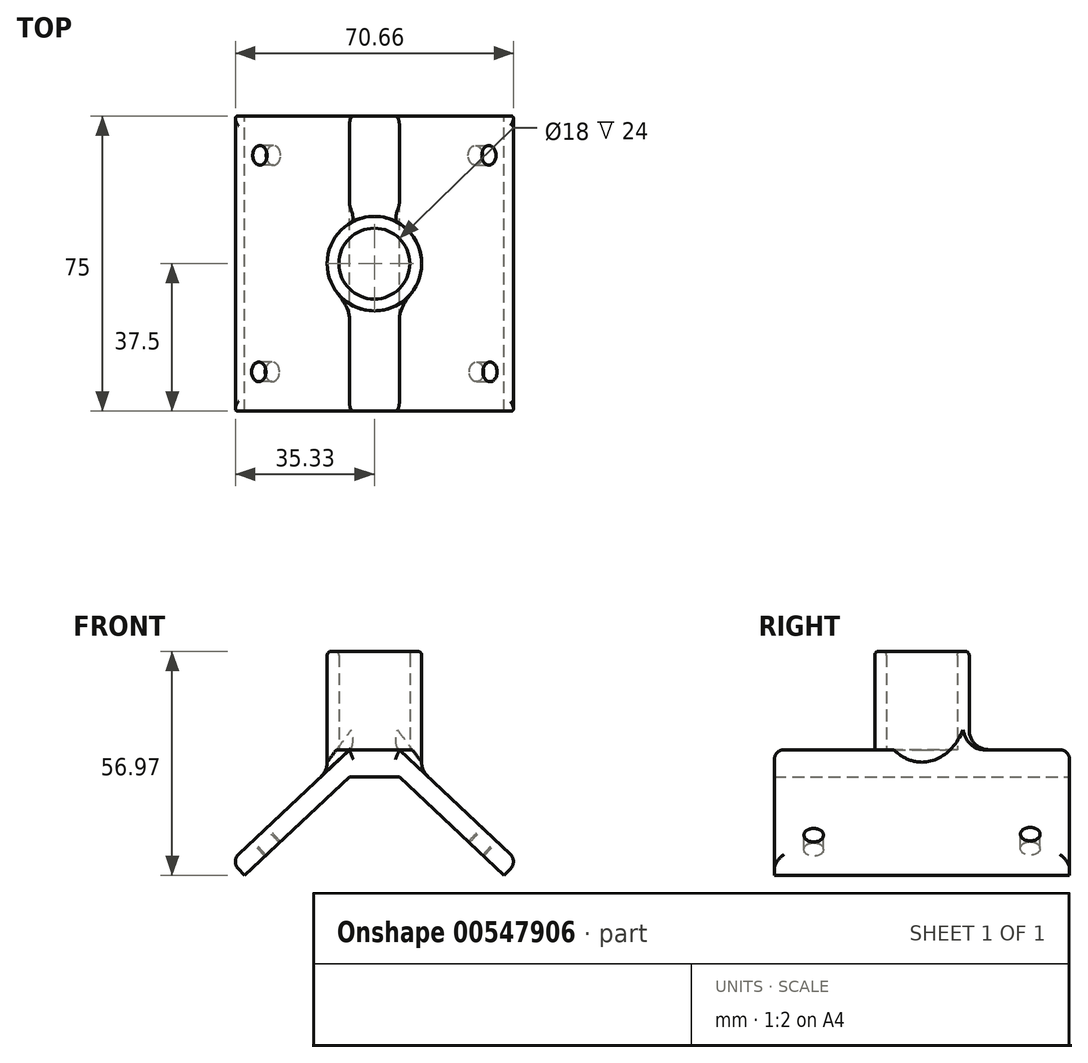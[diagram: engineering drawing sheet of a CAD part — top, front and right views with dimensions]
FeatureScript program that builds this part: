
annotation { "Feature Type Name" : "Feature", "Feature Type Description" : "" }
export const myFeature = defineFeature(function(context is Context, id is Id, definition is map)
    precondition{}
    {
        {
            var Q0;
            Q0=qCreatedBy(makeId("Front.planeOp"),FACE);
            var sketch = newSketch(context, id + "F0", { "sketchPlane" : qUnion([Q0])});
            skLineSegment(sketch, "E0", {"start": v(-6.35, 0) * mm, "end": v(6.35, 0) * mm});
            skLineSegment(sketch, "E1", {"start": v(6.35, 0) * mm, "end": v(107.95, -95.88) * mm});
            skLineSegment(sketch, "E2", {"start": v(107.95, -95.88) * mm, "end": v(-107.95, -95.88) * mm});
            skLineSegment(sketch, "E3", {"start": v(-107.95, -95.88) * mm, "end": v(-6.35, 0) * mm});
            skPoint(sketch, "E4", {"position": v(0, -95.88) * mm});
            skLineSegment(sketch, "E5", {"start": v(-32.93, -25.09) * mm, "end": v(-36.36, -21.45) * mm});
            skLineSegment(sketch, "E6", {"start": v(-36.36, -21.45) * mm, "end": v(0, 12.87) * mm});
            skLineSegment(sketch, "E7", {"start": v(0, 12.87) * mm, "end": v(0, 0) * mm});
            skLineSegment(sketch, "E8", {"start": v(-6.35, 6.88) * mm, "end": v(0, 6.88) * mm});
            skSolve(sketch);
        }
        {
            var Q0;
            {var subQ1=sQuery(id+"F0.wireOp",EDGE,"E5");Q0=makeQuery(id+"F0.imprint","IMPRINT",FACE,{"disambiguationData":[TD([[makeQuery(id+"F0.imprint","IMPRINT",EDGE,{"derivedFrom":subQ1}),-1.0]])]});}
            extrude(context, id + "F1", {"entities" : qUnion([Q0]), "endBound" : BoundingType.SYMMETRIC, "depth" : 75 * mm, "offsetDistance" : 25 * mm});
        }
        {
            var Q0;
            Q0=makeQuery(id+"F1.opExtrude","SWEPT_FACE",FACE,{"disambiguationData":[OSD([sQuery(id+"F0.wireOp",EDGE,"E6")])]});
            var sketch = newSketch(context, id + "F2", { "sketchPlane" : qUnion([Q0])});
            skLineSegment(sketch, "E9", {"start": v(-31.17, 37.5) * mm, "end": v(-31.17, 27.5) * mm, "construction": true});
            skLineSegment(sketch, "E10", {"start": v(-31.17, 27.5) * mm, "end": v(-41.17, 27.5) * mm, "construction": true});
            skCircle(sketch, "E11", {"center": v(-31.17, 27.5) * mm, "radius": 2.5 * mm});
            skLineSegment(sketch, "E12", {"start": v(-31.17, -37.5) * mm, "end": v(-31.55, -27.5) * mm, "construction": true});
            skLineSegment(sketch, "E13", {"start": v(-31.55, -27.5) * mm, "end": v(-41.17, -27.88) * mm, "construction": true});
            skCircle(sketch, "E14", {"center": v(-31.55, -27.5) * mm, "radius": 2.5 * mm});
            skSolve(sketch);
        }
        {
            var Q0;
            Q0=makeQuery(id+"F2.imprint","IMPRINT",FACE,{"disambiguationData":[TD([[makeQuery(id+"F2.imprint","IMPRINT",EDGE,{"derivedFrom":sQuery(id+"F2.wireOp",EDGE,"E11")}),1.0]])]});
            var Q1;
            Q1=makeQuery(id+"F2.imprint","IMPRINT",FACE,{"disambiguationData":[TD([[makeQuery(id+"F2.imprint","IMPRINT",EDGE,{"derivedFrom":sQuery(id+"F2.wireOp",EDGE,"E14")}),1.0]])]});
            extrude(context, id + "F3", {"entities" : qUnion([Q0, Q1]), "operationType" : NewBodyOperationType.REMOVE, "oppositeDirection" : true, "depth" : 25 * mm, "offsetDistance" : 25 * mm});
        }
        {
            var Q0;
            Q0=makeQuery(id+"F1.opExtrude","SWEPT_BODY",BODY,{"disambiguationData":[OSD([sQuery(id+"F0.wireOp",EDGE,"E0"),sQuery(id+"F0.wireOp",EDGE,"E3"),sQuery(id+"F0.wireOp",EDGE,"E5"),sQuery(id+"F0.wireOp",EDGE,"E6"),sQuery(id+"F0.wireOp",EDGE,"E7"),sQuery(id+"F0.wireOp",EDGE,"E8")])]});
            var Q1;
            Q1=qCreatedBy(makeId("Right.planeOp"),FACE);
            mirror(context, id + "F4", {"operationType" : NewBodyOperationType.ADD, "entities" : qUnion([Q0]), "mirrorPlane" : qUnion([Q1])});
        }
        {
            var Q0;
            {var subQ0=makeQuery(id+"F1.opExtrude","SWEPT_FACE",FACE,{"disambiguationData":[OSD([sQuery(id+"F0.wireOp",EDGE,"E8")])]});Q0=makeQuery(id+"F4.boolean.opBoolean","MERGE",FACE,{"derivedFrom":[subQ0,makeQuery(id+"F4.opPattern","COPY",FACE,{"derivedFrom":subQ0,"instanceName":"1"})]});}
            var sketch = newSketch(context, id + "F5", { "sketchPlane" : qUnion([Q0])});
            skCircle(sketch, "E15", {"center": v(0, 0) * mm, "radius": 9 * mm});
            skCircle(sketch, "E16", {"center": v(0, 0) * mm, "radius": 12 * mm});
            skSolve(sketch);
        }
        {
            var Q0;
            {var subQ0=sQuery(id+"F5.wireOp",EDGE,"E15");var subQ1=makeQuery(id+"F4.opPattern","COPY",EDGE,{"derivedFrom":makeQuery(id+"F1.opExtrude","SWEPT_EDGE",EDGE,{"disambiguationData":[OSD([sQuery(id+"F0.wireOp",EDGE,"E6"),sQuery(id+"F0.wireOp",EDGE,"E8")])]}),"instanceName":"1"});var subQ2=makeQuery(id+"F5.imprint","INTERSECT",VERTEX,{"disambiguationData":[OD(0.0)],"derivedFrom":[subQ1,subQ0]});Q0=makeQuery(id+"F5.imprint","IMPRINT",FACE,{"disambiguationData":[TD([[makeQuery(id+"F5.imprint","IMPRINT",EDGE,{"disambiguationData":[TD([[subQ2,1.0]])],"derivedFrom":subQ0}),-1.0]])]});}
            var Q1;
            {var subQ0=sQuery(id+"F5.wireOp",EDGE,"E15");var subQ1=makeQuery(id+"F1.opExtrude","SWEPT_EDGE",EDGE,{"disambiguationData":[OSD([sQuery(id+"F0.wireOp",EDGE,"E6"),sQuery(id+"F0.wireOp",EDGE,"E8")])]});var subQ2=makeQuery(id+"F5.imprint","INTERSECT",VERTEX,{"disambiguationData":[OD(1.0)],"derivedFrom":[subQ1,subQ0]});Q1=makeQuery(id+"F5.imprint","IMPRINT",FACE,{"disambiguationData":[TD([[makeQuery(id+"F5.imprint","IMPRINT",EDGE,{"disambiguationData":[TD([[subQ2,-1.0]])],"derivedFrom":subQ0}),-1.0]])]});}
            var Q2;
            {var subQ0=sQuery(id+"F5.wireOp",EDGE,"E15");var subQ1=makeQuery(id+"F1.opExtrude","SWEPT_EDGE",EDGE,{"disambiguationData":[OSD([sQuery(id+"F0.wireOp",EDGE,"E6"),sQuery(id+"F0.wireOp",EDGE,"E8")])]});var subQ2=makeQuery(id+"F5.imprint","INTERSECT",VERTEX,{"disambiguationData":[OD(0.0)],"derivedFrom":[subQ1,subQ0]});Q2=makeQuery(id+"F5.imprint","IMPRINT",FACE,{"disambiguationData":[TD([[makeQuery(id+"F5.imprint","IMPRINT",EDGE,{"disambiguationData":[TD([[subQ2,1.0]])],"derivedFrom":subQ0}),-1.0]])]});}
            var Q3;
            {var subQ0=sQuery(id+"F5.wireOp",EDGE,"E15");var subQ1=makeQuery(id+"F1.opExtrude","SWEPT_EDGE",EDGE,{"disambiguationData":[OSD([sQuery(id+"F0.wireOp",EDGE,"E6"),sQuery(id+"F0.wireOp",EDGE,"E8")])]});var subQ2=makeQuery(id+"F5.imprint","INTERSECT",VERTEX,{"disambiguationData":[OD(0.0)],"derivedFrom":[subQ1,subQ0]});Q3=makeQuery(id+"F5.imprint","IMPRINT",FACE,{"disambiguationData":[TD([[makeQuery(id+"F5.imprint","IMPRINT",EDGE,{"disambiguationData":[TD([[subQ2,-1.0]])],"derivedFrom":subQ0}),-1.0]])]});}
            var Q4;
            {var subQ0=sQuery(id+"F5.wireOp",EDGE,"E15");var subQ1=makeQuery(id+"F1.opExtrude","SWEPT_EDGE",EDGE,{"disambiguationData":[OSD([sQuery(id+"F0.wireOp",EDGE,"E6"),sQuery(id+"F0.wireOp",EDGE,"E8")])]});var subQ2=makeQuery(id+"F5.imprint","INTERSECT",VERTEX,{"disambiguationData":[OD(0.0)],"derivedFrom":[subQ1,subQ0]});Q4=makeQuery(id+"F5.imprint","IMPRINT",FACE,{"disambiguationData":[TD([[makeQuery(id+"F5.imprint","IMPRINT",EDGE,{"disambiguationData":[TD([[subQ2,-1.0]])],"derivedFrom":subQ0}),1.0]])]});}
            var Q5;
            {var subQ0=sQuery(id+"F5.wireOp",EDGE,"E15");var subQ1=makeQuery(id+"F4.opPattern","COPY",EDGE,{"derivedFrom":makeQuery(id+"F1.opExtrude","SWEPT_EDGE",EDGE,{"disambiguationData":[OSD([sQuery(id+"F0.wireOp",EDGE,"E6"),sQuery(id+"F0.wireOp",EDGE,"E8")])]}),"instanceName":"1"});var subQ2=makeQuery(id+"F5.imprint","INTERSECT",VERTEX,{"disambiguationData":[OD(0.0)],"derivedFrom":[subQ1,subQ0]});Q5=makeQuery(id+"F5.imprint","IMPRINT",FACE,{"disambiguationData":[TD([[makeQuery(id+"F5.imprint","IMPRINT",EDGE,{"disambiguationData":[TD([[subQ2,1.0]])],"derivedFrom":subQ0}),1.0]])]});}
            var Q6;
            {var subQ0=makeQuery(id+"F1.opExtrude","SWEPT_FACE",FACE,{"disambiguationData":[OSD([sQuery(id+"F0.wireOp",EDGE,"E0")])]});Q6=makeQuery(id+"F4.boolean.opBoolean","MERGE",FACE,{"derivedFrom":[subQ0,makeQuery(id+"F4.opPattern","COPY",FACE,{"derivedFrom":subQ0,"instanceName":"1"})]});}
            extrude(context, id + "F6", {"entities" : qUnion([Q0, Q1, Q2, Q3, Q4, Q5]), "operationType" : NewBodyOperationType.ADD, "endBound" : BoundingType.UP_TO_SURFACE, "oppositeDirection" : true, "depth" : 25 * mm, "endBoundEntityFace" : qUnion([Q6]), "offsetDistance" : 25 * mm});
        }
        {
            var Q0;
            {var subQ0=sQuery(id+"F5.wireOp",EDGE,"E15");var subQ1=makeQuery(id+"F1.opExtrude","SWEPT_EDGE",EDGE,{"disambiguationData":[OSD([sQuery(id+"F0.wireOp",EDGE,"E6"),sQuery(id+"F0.wireOp",EDGE,"E8")])]});var subQ2=makeQuery(id+"F5.imprint","INTERSECT",VERTEX,{"disambiguationData":[OD(0.0)],"derivedFrom":[subQ1,subQ0]});Q0=makeQuery(id+"F5.imprint","IMPRINT",FACE,{"disambiguationData":[TD([[makeQuery(id+"F5.imprint","IMPRINT",EDGE,{"disambiguationData":[TD([[subQ2,-1.0]])],"derivedFrom":subQ0}),-1.0]])]});}
            var Q1;
            {var subQ0=sQuery(id+"F5.wireOp",EDGE,"E15");var subQ1=makeQuery(id+"F1.opExtrude","SWEPT_EDGE",EDGE,{"disambiguationData":[OSD([sQuery(id+"F0.wireOp",EDGE,"E6"),sQuery(id+"F0.wireOp",EDGE,"E8")])]});var subQ2=makeQuery(id+"F5.imprint","INTERSECT",VERTEX,{"disambiguationData":[OD(0.0)],"derivedFrom":[subQ1,subQ0]});Q1=makeQuery(id+"F5.imprint","IMPRINT",FACE,{"disambiguationData":[TD([[makeQuery(id+"F5.imprint","IMPRINT",EDGE,{"disambiguationData":[TD([[subQ2,1.0]])],"derivedFrom":subQ0}),-1.0]])]});}
            var Q2;
            {var subQ0=sQuery(id+"F5.wireOp",EDGE,"E15");var subQ1=makeQuery(id+"F4.opPattern","COPY",EDGE,{"derivedFrom":makeQuery(id+"F1.opExtrude","SWEPT_EDGE",EDGE,{"disambiguationData":[OSD([sQuery(id+"F0.wireOp",EDGE,"E6"),sQuery(id+"F0.wireOp",EDGE,"E8")])]}),"instanceName":"1"});var subQ2=makeQuery(id+"F5.imprint","INTERSECT",VERTEX,{"disambiguationData":[OD(0.0)],"derivedFrom":[subQ1,subQ0]});Q2=makeQuery(id+"F5.imprint","IMPRINT",FACE,{"disambiguationData":[TD([[makeQuery(id+"F5.imprint","IMPRINT",EDGE,{"disambiguationData":[TD([[subQ2,1.0]])],"derivedFrom":subQ0}),-1.0]])]});}
            var Q3;
            {var subQ0=sQuery(id+"F5.wireOp",EDGE,"E15");var subQ1=makeQuery(id+"F1.opExtrude","SWEPT_EDGE",EDGE,{"disambiguationData":[OSD([sQuery(id+"F0.wireOp",EDGE,"E6"),sQuery(id+"F0.wireOp",EDGE,"E8")])]});var subQ2=makeQuery(id+"F5.imprint","INTERSECT",VERTEX,{"disambiguationData":[OD(1.0)],"derivedFrom":[subQ1,subQ0]});Q3=makeQuery(id+"F5.imprint","IMPRINT",FACE,{"disambiguationData":[TD([[makeQuery(id+"F5.imprint","IMPRINT",EDGE,{"disambiguationData":[TD([[subQ2,-1.0]])],"derivedFrom":subQ0}),-1.0]])]});}
            extrude(context, id + "F7", {"entities" : qUnion([Q0, Q1, Q2, Q3]), "operationType" : NewBodyOperationType.ADD, "depth" : 25 * mm, "offsetDistance" : 25 * mm});
        }
        {
            var Q0;
            Q0=makeQuery(id+"F7.opExtrude","CAP_EDGE",EDGE,{"disambiguationData":[OSD([sQuery(id+"F5.wireOp",EDGE,"E16")])],"isStart":false});
            var Q1;
            Q1=makeQuery(id+"F7.opExtrude","CAP_EDGE",EDGE,{"disambiguationData":[OSD([sQuery(id+"F5.wireOp",EDGE,"E15")])],"isStart":false});
            fillet(context, id + "F8", {"entities" : qUnion([Q0, Q1]), "tangentPropagation" : true, "radius" : 1 * mm, "defaultsChanged" : false, "vertexSettings" : [], "allowEdgeOverflow" : false});
        }
        {
            var Q0;
            Q0=makeQuery(id+"F6.boolean.opBoolean","INTERSECT",EDGE,{"derivedFrom":[makeQuery(id+"F1.opExtrude","SWEPT_FACE",FACE,{"disambiguationData":[OSD([sQuery(id+"F0.wireOp",EDGE,"E6")])]}),makeQuery(id+"F6.opExtrude","SWEPT_FACE",FACE,{"disambiguationData":[OSD([sQuery(id+"F5.wireOp",EDGE,"E16")])]})]});
            var Q1;
            Q1=makeQuery(id+"F7.boolean.opBoolean","SPLIT",EDGE,{"disambiguationData":[OD(1.0)],"derivedFrom":makeQuery(id+"F7.opExtrude","CAP_EDGE",EDGE,{"disambiguationData":[OSD([sQuery(id+"F5.wireOp",EDGE,"E16")])],"isStart":true})});
            var Q2;
            Q2=makeQuery(id+"F6.boolean.opBoolean","INTERSECT",EDGE,{"derivedFrom":[makeQuery(id+"F4.opPattern","COPY",FACE,{"derivedFrom":makeQuery(id+"F1.opExtrude","SWEPT_FACE",FACE,{"disambiguationData":[OSD([sQuery(id+"F0.wireOp",EDGE,"E6")])]}),"instanceName":"1"}),makeQuery(id+"F6.opExtrude","SWEPT_FACE",FACE,{"disambiguationData":[OSD([sQuery(id+"F5.wireOp",EDGE,"E16")])]})]});
            var Q3;
            Q3=makeQuery(id+"F7.boolean.opBoolean","SPLIT",EDGE,{"disambiguationData":[OD(0.0)],"derivedFrom":makeQuery(id+"F7.opExtrude","CAP_EDGE",EDGE,{"disambiguationData":[OSD([sQuery(id+"F5.wireOp",EDGE,"E16")])],"isStart":true})});
            fillet(context, id + "F9", {"entities" : qUnion([Q0, Q1, Q2, Q3]), "tangentPropagation" : true, "radius" : 5 * mm, "defaultsChanged" : false, "vertexSettings" : [], "allowEdgeOverflow" : false});
        }
        {
            var Q0;
            Q0=makeQuery(id+"F1.opExtrude","CAP_EDGE",EDGE,{"disambiguationData":[OSD([sQuery(id+"F0.wireOp",EDGE,"E6")])],"isStart":true});
            var Q1;
            Q1=makeQuery(id+"F1.opExtrude","SWEPT_EDGE",EDGE,{"disambiguationData":[OSD([sQuery(id+"F0.wireOp",EDGE,"E5"),sQuery(id+"F0.wireOp",EDGE,"E6")])]});
            var Q2;
            Q2=makeQuery(id+"F1.opExtrude","CAP_EDGE",EDGE,{"disambiguationData":[OSD([sQuery(id+"F0.wireOp",EDGE,"E6")])],"isStart":false});
            var Q3;
            {var subQ0=makeQuery(id+"F1.opExtrude","CAP_EDGE",EDGE,{"disambiguationData":[OSD([sQuery(id+"F0.wireOp",EDGE,"E8")])],"isStart":false});Q3=makeQuery(id+"F4.boolean.opBoolean","MERGE",EDGE,{"derivedFrom":[subQ0,makeQuery(id+"F4.opPattern","COPY",EDGE,{"derivedFrom":subQ0,"instanceName":"1"})]});}
            var Q4;
            Q4=makeQuery(id+"F4.opPattern","COPY",EDGE,{"derivedFrom":makeQuery(id+"F1.opExtrude","CAP_EDGE",EDGE,{"disambiguationData":[OSD([sQuery(id+"F0.wireOp",EDGE,"E6")])],"isStart":false}),"instanceName":"1"});
            var Q5;
            Q5=makeQuery(id+"F4.opPattern","COPY",EDGE,{"derivedFrom":makeQuery(id+"F1.opExtrude","SWEPT_EDGE",EDGE,{"disambiguationData":[OSD([sQuery(id+"F0.wireOp",EDGE,"E5"),sQuery(id+"F0.wireOp",EDGE,"E6")])]}),"instanceName":"1"});
            var Q6;
            Q6=makeQuery(id+"F4.opPattern","COPY",EDGE,{"derivedFrom":makeQuery(id+"F1.opExtrude","CAP_EDGE",EDGE,{"disambiguationData":[OSD([sQuery(id+"F0.wireOp",EDGE,"E6")])],"isStart":true}),"instanceName":"1"});
            var Q7;
            {var subQ0=makeQuery(id+"F1.opExtrude","CAP_EDGE",EDGE,{"disambiguationData":[OSD([sQuery(id+"F0.wireOp",EDGE,"E8")])],"isStart":true});Q7=makeQuery(id+"F4.boolean.opBoolean","MERGE",EDGE,{"derivedFrom":[subQ0,makeQuery(id+"F4.opPattern","COPY",EDGE,{"derivedFrom":subQ0,"instanceName":"1"})]});}
            fillet(context, id + "F10", {"entities" : qUnion([Q0, Q1, Q2, Q3, Q4, Q5, Q6, Q7]), "tangentPropagation" : true, "radius" : 2.5 * mm, "defaultsChanged" : false, "vertexSettings" : [], "allowEdgeOverflow" : false});
        }
    });
